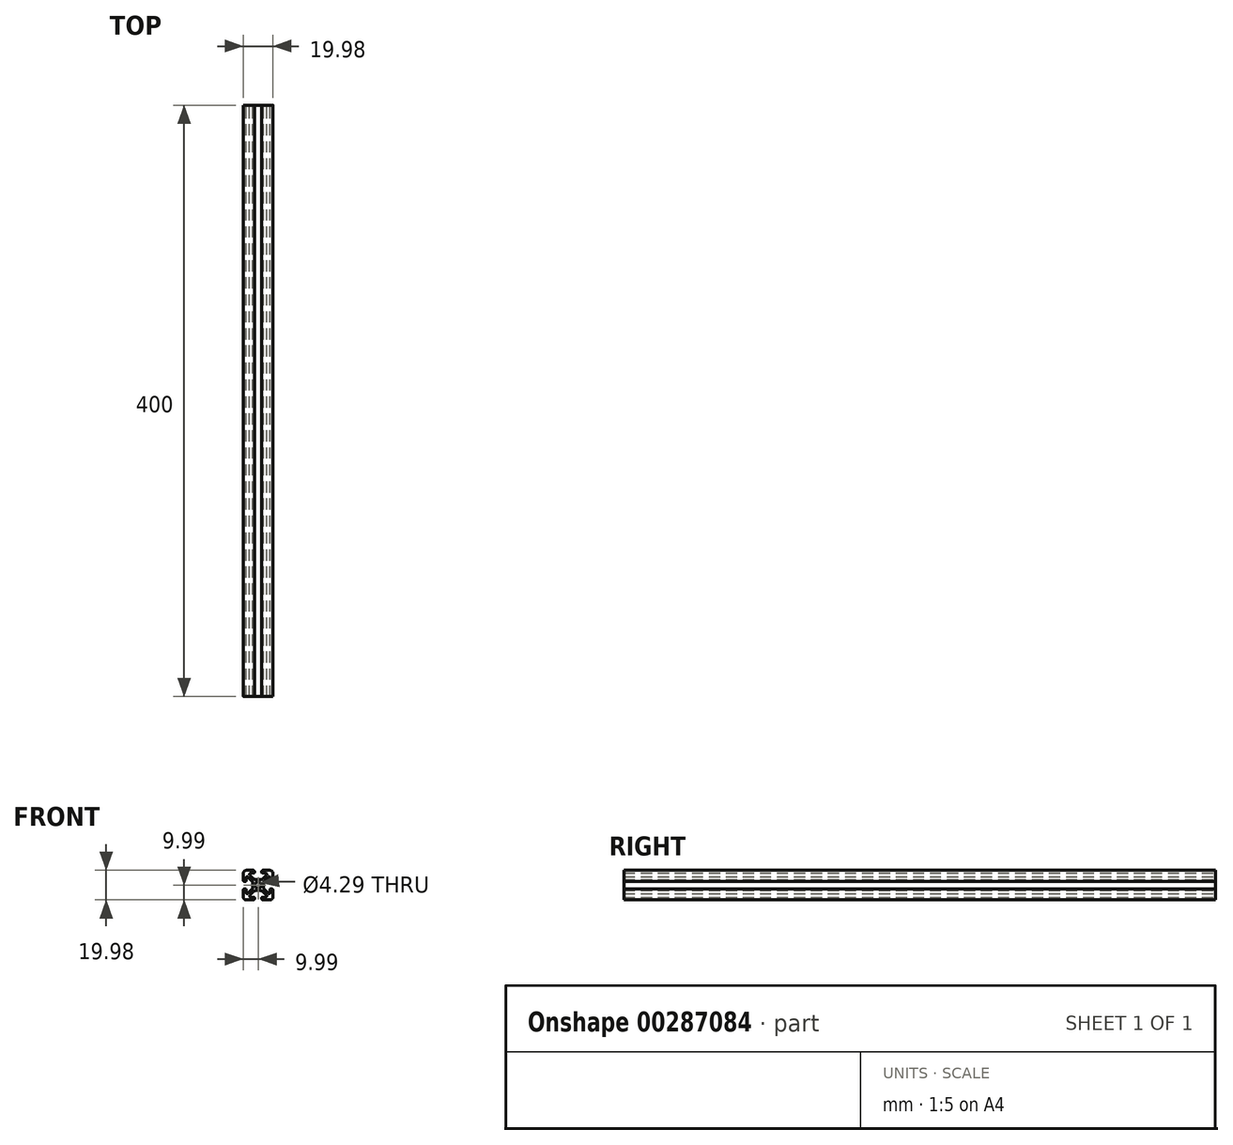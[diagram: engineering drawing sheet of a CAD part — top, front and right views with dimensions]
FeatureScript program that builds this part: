
annotation { "Feature Type Name" : "Feature", "Feature Type Description" : "" }
export const myFeature = defineFeature(function(context is Context, id is Id, definition is map)
    precondition{}
    {
        {
            var Q0;
            Q0=qCreatedBy(makeId("Front.planeOp"),FACE);
            var sketch = newSketch(context, id + "F0", { "sketchPlane" : qUnion([Q0])});
            skLineSegment(sketch, "E0", {"start": v(-7.99, 10) * mm, "end": v(-3.29, 10) * mm});
            skArc(sketch, "E1", {"start": v(-3.29, 10) * mm, "mid": v(-2.73, 9.76) * mm, "end": v(-2.5, 9.2) * mm});
            skLineSegment(sketch, "E2", {"start": v(-2.5, 9.2) * mm, "end": v(-2.5, 8.5) * mm});
            skLineSegment(sketch, "E3", {"start": v(-5.5, 6.76) * mm, "end": v(-3.25, 4.5) * mm});
            skArc(sketch, "E4", {"start": v(-4.91, 8.2) * mm, "mid": v(-5.69, 7.67) * mm, "end": v(-5.5, 6.76) * mm});
            skLineSegment(sketch, "E5", {"start": v(3.29, 10) * mm, "end": v(7.99, 10) * mm});
            skArc(sketch, "E6", {"start": v(2.5, 9.2) * mm, "mid": v(2.73, 9.76) * mm, "end": v(3.29, 10) * mm});
            skLineSegment(sketch, "E7", {"start": v(3.25, 4.5) * mm, "end": v(5.5, 6.76) * mm});
            skArc(sketch, "E8", {"start": v(1.13, 3.63) * mm, "mid": v(2.28, 3.86) * mm, "end": v(3.25, 4.5) * mm});
            skArc(sketch, "E9", {"start": v(7.99, 10) * mm, "mid": v(9.4, 9.4) * mm, "end": v(10, 7.99) * mm});
            skLineSegment(sketch, "E10", {"start": v(-2.8, 8.2) * mm, "end": v(-4.91, 8.2) * mm});
            skArc(sketch, "E11", {"start": v(-2.5, 8.5) * mm, "mid": v(-2.6, 8.28) * mm, "end": v(-2.8, 8.2) * mm});
            skLineSegment(sketch, "E12", {"start": v(4.91, 8.2) * mm, "end": v(2.8, 8.2) * mm});
            skLineSegment(sketch, "E13", {"start": v(2.5, 8.5) * mm, "end": v(2.5, 9.2) * mm});
            skArc(sketch, "E14", {"start": v(2.8, 8.2) * mm, "mid": v(2.6, 8.28) * mm, "end": v(2.5, 8.5) * mm});
            skArc(sketch, "E15", {"start": v(5.5, 6.76) * mm, "mid": v(5.69, 7.67) * mm, "end": v(4.91, 8.2) * mm});
            skLineSegment(sketch, "E16", {"start": v(-1.13, 3.63) * mm, "end": v(1.13, 3.63) * mm});
            skArc(sketch, "E17", {"start": v(-3.25, 4.5) * mm, "mid": v(-2.28, 3.86) * mm, "end": v(-1.13, 3.63) * mm});
            skArc(sketch, "E18", {"start": v(-10, 7.99) * mm, "mid": v(-9.4, 9.4) * mm, "end": v(-7.99, 10) * mm});
            skLineSegment(sketch, "E19", {"start": v(10, 7.99) * mm, "end": v(10, 3.29) * mm});
            skLineSegment(sketch, "E20", {"start": v(4.5, -3.25) * mm, "end": v(6.76, -5.5) * mm});
            skArc(sketch, "E21", {"start": v(3.63, -1.13) * mm, "mid": v(3.86, -2.28) * mm, "end": v(4.5, -3.25) * mm});
            skLineSegment(sketch, "E22", {"start": v(3.63, 1.13) * mm, "end": v(3.63, -1.13) * mm});
            skArc(sketch, "E23", {"start": v(9.2, -2.5) * mm, "mid": v(9.76, -2.73) * mm, "end": v(10, -3.29) * mm});
            skLineSegment(sketch, "E24", {"start": v(10, -3.29) * mm, "end": v(10, -7.99) * mm});
            skLineSegment(sketch, "E25", {"start": v(8.5, -2.5) * mm, "end": v(9.2, -2.5) * mm});
            skLineSegment(sketch, "E26", {"start": v(-9.2, -2.5) * mm, "end": v(-8.5, -2.5) * mm});
            skArc(sketch, "E27", {"start": v(-10, -3.29) * mm, "mid": v(-9.76, -2.73) * mm, "end": v(-9.2, -2.5) * mm});
            skLineSegment(sketch, "E28", {"start": v(-8.2, -2.8) * mm, "end": v(-8.2, -4.91) * mm});
            skLineSegment(sketch, "E29", {"start": v(-10, 3.29) * mm, "end": v(-10, 7.99) * mm});
            skArc(sketch, "E30", {"start": v(-9.2, 2.5) * mm, "mid": v(-9.76, 2.73) * mm, "end": v(-10, 3.29) * mm});
            skLineSegment(sketch, "E31", {"start": v(-4.5, 3.25) * mm, "end": v(-6.76, 5.5) * mm});
            skLineSegment(sketch, "E32", {"start": v(-3.63, -1.13) * mm, "end": v(-3.63, 1.13) * mm});
            skArc(sketch, "E33", {"start": v(-3.63, 1.13) * mm, "mid": v(-3.86, 2.28) * mm, "end": v(-4.5, 3.25) * mm});
            skArc(sketch, "E34", {"start": v(-6.76, 5.5) * mm, "mid": v(-7.67, 5.69) * mm, "end": v(-8.2, 4.91) * mm});
            skLineSegment(sketch, "E35", {"start": v(-8.5, 2.5) * mm, "end": v(-9.2, 2.5) * mm});
            skLineSegment(sketch, "E36", {"start": v(8.2, 2.8) * mm, "end": v(8.2, 4.91) * mm});
            skArc(sketch, "E37", {"start": v(8.2, 4.91) * mm, "mid": v(7.67, 5.69) * mm, "end": v(6.76, 5.5) * mm});
            skLineSegment(sketch, "E38", {"start": v(-10, -7.99) * mm, "end": v(-10, -3.29) * mm});
            skArc(sketch, "E39", {"start": v(-4.5, -3.25) * mm, "mid": v(-3.86, -2.28) * mm, "end": v(-3.63, -1.13) * mm});
            skLineSegment(sketch, "E40", {"start": v(-6.76, -5.5) * mm, "end": v(-4.5, -3.25) * mm});
            skLineSegment(sketch, "E41", {"start": v(1.13, -3.63) * mm, "end": v(-1.13, -3.63) * mm});
            skLineSegment(sketch, "E42", {"start": v(5.5, -6.76) * mm, "end": v(3.25, -4.5) * mm});
            skArc(sketch, "E43", {"start": v(3.25, -4.5) * mm, "mid": v(2.28, -3.86) * mm, "end": v(1.13, -3.63) * mm});
            skLineSegment(sketch, "E44", {"start": v(8.2, -4.91) * mm, "end": v(8.2, -2.8) * mm});
            skLineSegment(sketch, "E45", {"start": v(-4.91, -8.2) * mm, "end": v(-2.8, -8.2) * mm});
            skArc(sketch, "E46", {"start": v(-5.5, -6.76) * mm, "mid": v(-5.69, -7.67) * mm, "end": v(-4.91, -8.2) * mm});
            skArc(sketch, "E47", {"start": v(-8.2, -4.91) * mm, "mid": v(-7.67, -5.69) * mm, "end": v(-6.76, -5.5) * mm});
            skArc(sketch, "E48", {"start": v(-8.5, -2.5) * mm, "mid": v(-8.28, -2.6) * mm, "end": v(-8.2, -2.8) * mm});
            skArc(sketch, "E49", {"start": v(4.91, -8.2) * mm, "mid": v(5.69, -7.67) * mm, "end": v(5.5, -6.76) * mm});
            skLineSegment(sketch, "E50", {"start": v(2.5, -9.2) * mm, "end": v(2.5, -8.5) * mm});
            skArc(sketch, "E51", {"start": v(2.5, -8.5) * mm, "mid": v(2.6, -8.28) * mm, "end": v(2.8, -8.2) * mm});
            skLineSegment(sketch, "E52", {"start": v(2.8, -8.2) * mm, "end": v(4.91, -8.2) * mm});
            skArc(sketch, "E53", {"start": v(3.29, -10) * mm, "mid": v(2.73, -9.76) * mm, "end": v(2.5, -9.2) * mm});
            skArc(sketch, "E54", {"start": v(6.76, -5.5) * mm, "mid": v(7.67, -5.69) * mm, "end": v(8.2, -4.91) * mm});
            skArc(sketch, "E55", {"start": v(10, -7.99) * mm, "mid": v(9.4, -9.4) * mm, "end": v(7.99, -10) * mm});
            skArc(sketch, "E56", {"start": v(4.5, 3.25) * mm, "mid": v(3.86, 2.28) * mm, "end": v(3.63, 1.13) * mm});
            skLineSegment(sketch, "E57", {"start": v(-3.25, -4.5) * mm, "end": v(-5.5, -6.76) * mm});
            skLineSegment(sketch, "E58", {"start": v(-2.5, -8.5) * mm, "end": v(-2.5, -9.2) * mm});
            skArc(sketch, "E59", {"start": v(-2.8, -8.2) * mm, "mid": v(-2.6, -8.28) * mm, "end": v(-2.5, -8.5) * mm});
            skArc(sketch, "E60", {"start": v(-2.5, -9.2) * mm, "mid": v(-2.73, -9.76) * mm, "end": v(-3.29, -10) * mm});
            skArc(sketch, "E61", {"start": v(-1.13, -3.63) * mm, "mid": v(-2.28, -3.86) * mm, "end": v(-3.25, -4.5) * mm});
            skArc(sketch, "E62", {"start": v(10, 3.29) * mm, "mid": v(9.76, 2.73) * mm, "end": v(9.2, 2.5) * mm});
            skLineSegment(sketch, "E63", {"start": v(6.76, 5.5) * mm, "end": v(4.5, 3.25) * mm});
            skLineSegment(sketch, "E64", {"start": v(-8.2, 4.91) * mm, "end": v(-8.2, 2.8) * mm});
            skLineSegment(sketch, "E65", {"start": v(-3.29, -10) * mm, "end": v(-7.99, -10) * mm});
            skArc(sketch, "E66", {"start": v(-7.99, -10) * mm, "mid": v(-9.4, -9.4) * mm, "end": v(-10, -7.99) * mm});
            skLineSegment(sketch, "E67", {"start": v(7.99, -10) * mm, "end": v(3.29, -10) * mm});
            skLineSegment(sketch, "E68", {"start": v(9.2, 2.5) * mm, "end": v(8.5, 2.5) * mm});
            skArc(sketch, "E69", {"start": v(8.5, 2.5) * mm, "mid": v(8.28, 2.6) * mm, "end": v(8.2, 2.8) * mm});
            skCircle(sketch, "E70", {"center": v(0, 0) * mm, "radius": 2.15 * mm});
            skArc(sketch, "E71", {"start": v(-8.2, 2.8) * mm, "mid": v(-8.28, 2.6) * mm, "end": v(-8.5, 2.5) * mm});
            skArc(sketch, "E72", {"start": v(8.2, -2.8) * mm, "mid": v(8.28, -2.6) * mm, "end": v(8.5, -2.5) * mm});
            skSolve(sketch);
        }
        {
            var Q0;
            Q0=qSketchRegion(id+"F0",true);
            extrude(context, id + "F1", {"entities" : qUnion([Q0]), "depth" : 400 * mm});
        }
    });
